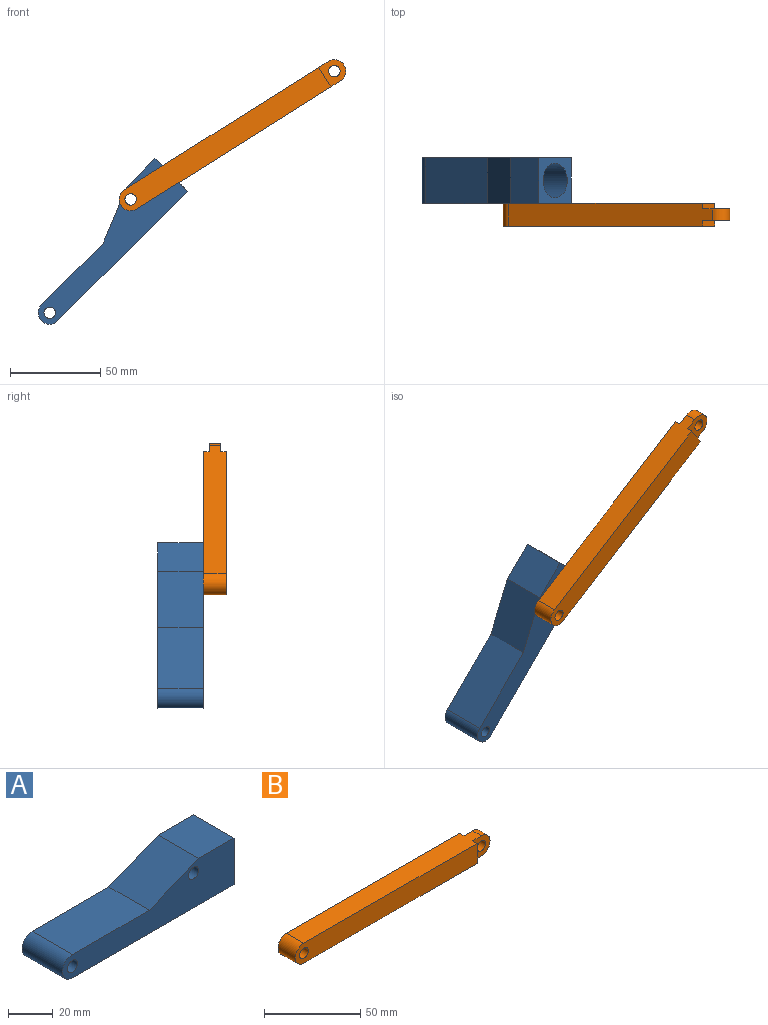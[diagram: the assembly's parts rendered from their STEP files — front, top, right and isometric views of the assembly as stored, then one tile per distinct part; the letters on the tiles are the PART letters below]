
ASSEMBLY  parts=2 mates=1
PART A: 12 faces, bbox 108x25.4x25.4 mm
  f0: plane 48.33x25.4mm, normal (0,0,1), area 1227.5mm2, adj f1,f7,f8,f9
  f1: cylinder r=6.35mm len=25.4mm, axis (0,1,0), area 506.7mm2, adj f0,f2,f8,f9
  f2: plane 101.6x25.4mm, normal (0,0,-1), area 2580.6mm2, adj f1,f3,f8,f9
  f3: plane 25.4x25.4mm, normal (1,0,0), area 360.1mm2, adj f2,f4,f8,f9,f10
  f4: plane 25.4x22.23mm, normal (0,0,1), area 564.5mm2, adj f3,f7,f8,f9
  f5: cylinder r=3.17mm len=25.4mm, axis (0,1,0), area 506.7mm2, adj f8,f9
  f6: cylinder r=3.17mm len=25.4mm, axis (0,1,0), area 506.7mm2, adj f8,f9
  f7: plane 31.05x25.4mm, normal (-0.38,0,0.93), area 852mm2, adj f0,f4,f8,f9
  f8: plane 107.95x25.4mm, normal (0,-1,0), area 1769.7mm2, adj f0,f1,f2,f3,f4,f5,f6,f7
  f9: plane 107.95x25.4mm, normal (0,1,0), area 1769.7mm2, adj f0,f1,f2,f3,f4,f5,f6,f7
  f10: cylinder r=9.53mm len=19.05mm, axis (1,0,0), area 1140.1mm2, adj f3,f11
  f11: plane 19.05x19.05mm, normal (1,0,0), area 285mm2, adj f10
PART B: 12 faces, bbox 146.1x12.7x12.7 mm
  f0: plane 12.7x3.18mm, normal (1,0,0), area 40.3mm2, adj f2,f5,f7,f11
  f1: cylinder r=6.35mm len=12.7mm, axis (0,1,0), area 253.4mm2, adj f2,f5,f6,f7
  f2: plane 133.35x12.7mm, normal (0,0,-1), area 1653.2mm2, adj f0,f1,f3,f6,f7,f8,f10,f11
  f3: plane 12.7x3.18mm, normal (1,0,0), area 40.3mm2, adj f2,f5,f6,f10
  f4: cylinder r=3.17mm len=12.7mm, axis (0,1,0), area 253.4mm2, adj f6,f7
  f5: plane 133.35x12.7mm, normal (0,0,1), area 1653.2mm2, adj f0,f1,f3,f6,f7,f8,f10,f11
  f6: plane 133.35x12.7mm, normal (0,-1,0), area 1644.6mm2, adj f1,f2,f3,f4,f5
  f7: plane 133.35x12.7mm, normal (0,1,0), area 1644.6mm2, adj f0,f1,f2,f4,f5
  f8: cylinder r=6.35mm len=12.7mm, axis (0,1,0), area 126.7mm2, adj f2,f5,f10,f11
  f9: cylinder r=3.17mm len=6.35mm, axis (0,1,0), area 126.7mm2, adj f10,f11
  f10: plane 12.7x12.7mm, normal (0,-1,0), area 112.3mm2, adj f2,f3,f5,f8,f9
  f11: plane 12.7x12.7mm, normal (0,1,0), area 112.3mm2, adj f0,f2,f5,f8,f9
PLACE A rot(axis=(0,-1,0),45deg) t=(-196.33,49.53,-111.49)mm
PLACE B rot(axis=(0,-1,0),32.2deg) t=(-151.43,17.78,-48.63)mm
MATE revolute A.f6 <-> B.f4  axis (0,-1,0) through (-151.43,24.13,-48.63)mm
